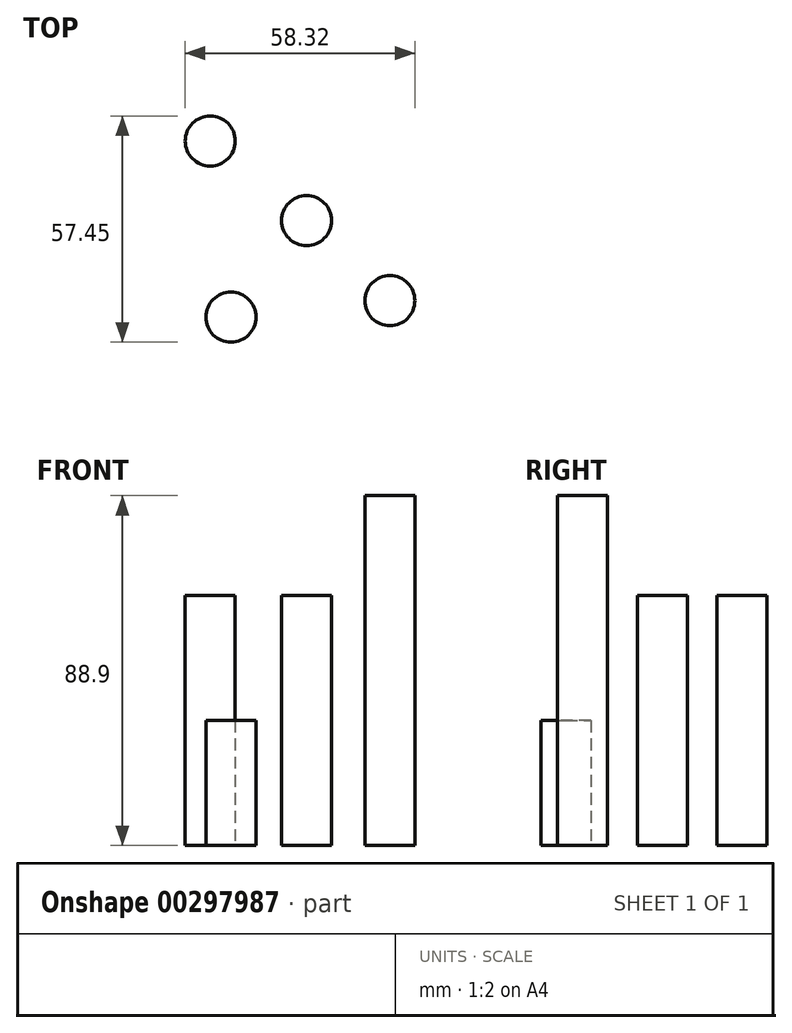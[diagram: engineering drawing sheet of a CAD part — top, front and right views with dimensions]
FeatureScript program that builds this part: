
annotation { "Feature Type Name" : "Feature", "Feature Type Description" : "" }
export const myFeature = defineFeature(function(context is Context, id is Id, definition is map)
    precondition{}
    {
        {
            var Q0;
            Q0=qCreatedBy(makeId("Top.planeOp"),FACE);
            var sketch = newSketch(context, id + "F0", { "sketchPlane" : qUnion([Q0])});
            skCircle(sketch, "E0", {"center": v(-131.3, 7.18) * mm, "radius": 6.35 * mm});
            skCircle(sketch, "E1.MirrorC", {"center": v(-106.84, 7.18) * mm, "radius": 6.35 * mm});
            skCircle(sketch, "E2.MirrorC", {"center": v(-131.3, -13.05) * mm, "radius": 6.35 * mm});
            skCircle(sketch, "E3.MirrorC", {"center": v(-106.84, -13.05) * mm, "radius": 6.35 * mm});
            skCircle(sketch, "E4", {"center": v(-126.06, -37.57) * mm, "radius": 6.35 * mm});
            skCircle(sketch, "E5.MirrorC", {"center": v(-85.68, -33.39) * mm, "radius": 6.35 * mm});
            skSolve(sketch);
        }
        {
            var Q0;
            Q0=makeQuery(id+"F0.imprint","IMPRINT",FACE,{"disambiguationData":[TD([[makeQuery(id+"F0.imprint","IMPRINT",EDGE,{"derivedFrom":sQuery(id+"F0.wireOp",EDGE,"E0")}),1.0]])]});
            extrude(context, id + "F1", {"entities" : qUnion([Q0]), "depth" : 63.5 * mm});
        }
        {
            var Q0;
            Q0=makeQuery(id+"F0.imprint","IMPRINT",FACE,{"disambiguationData":[TD([[makeQuery(id+"F0.imprint","IMPRINT",EDGE,{"derivedFrom":sQuery(id+"F0.wireOp",EDGE,"E1.MirrorC")}),-1.0]])]});
            var Q1;
            Q1=makeQuery(id+"F0.imprint","IMPRINT",FACE,{"disambiguationData":[TD([[makeQuery(id+"F0.imprint","IMPRINT",EDGE,{"derivedFrom":sQuery(id+"F0.wireOp",EDGE,"E2.MirrorC")}),-1.0]])]});
            var Q2;
            Q2=makeQuery(id+"F0.imprint","IMPRINT",FACE,{"disambiguationData":[TD([[makeQuery(id+"F0.imprint","IMPRINT",EDGE,{"derivedFrom":sQuery(id+"F0.wireOp",EDGE,"E3.MirrorC")}),1.0]])]});
            extrude(context, id + "F2", {"entities" : qUnion([Q0, Q1, Q2]), "operationType" : NewBodyOperationType.ADD, "depth" : 63.5 * mm});
        }
        {
            var Q0;
            Q0=makeQuery(id+"F0.imprint","IMPRINT",FACE,{"disambiguationData":[TD([[makeQuery(id+"F0.imprint","IMPRINT",EDGE,{"derivedFrom":sQuery(id+"F0.wireOp",EDGE,"E4")}),1.0]])]});
            extrude(context, id + "F3", {"entities" : qUnion([Q0]), "depth" : 31.75 * mm});
        }
        {
            var Q0;
            Q0=makeQuery(id+"F0.imprint","IMPRINT",FACE,{"disambiguationData":[TD([[makeQuery(id+"F0.imprint","IMPRINT",EDGE,{"derivedFrom":sQuery(id+"F0.wireOp",EDGE,"E5.MirrorC")}),1.0]])]});
            extrude(context, id + "F4", {"entities" : qUnion([Q0]), "depth" : 88.9 * mm});
        }
    });
